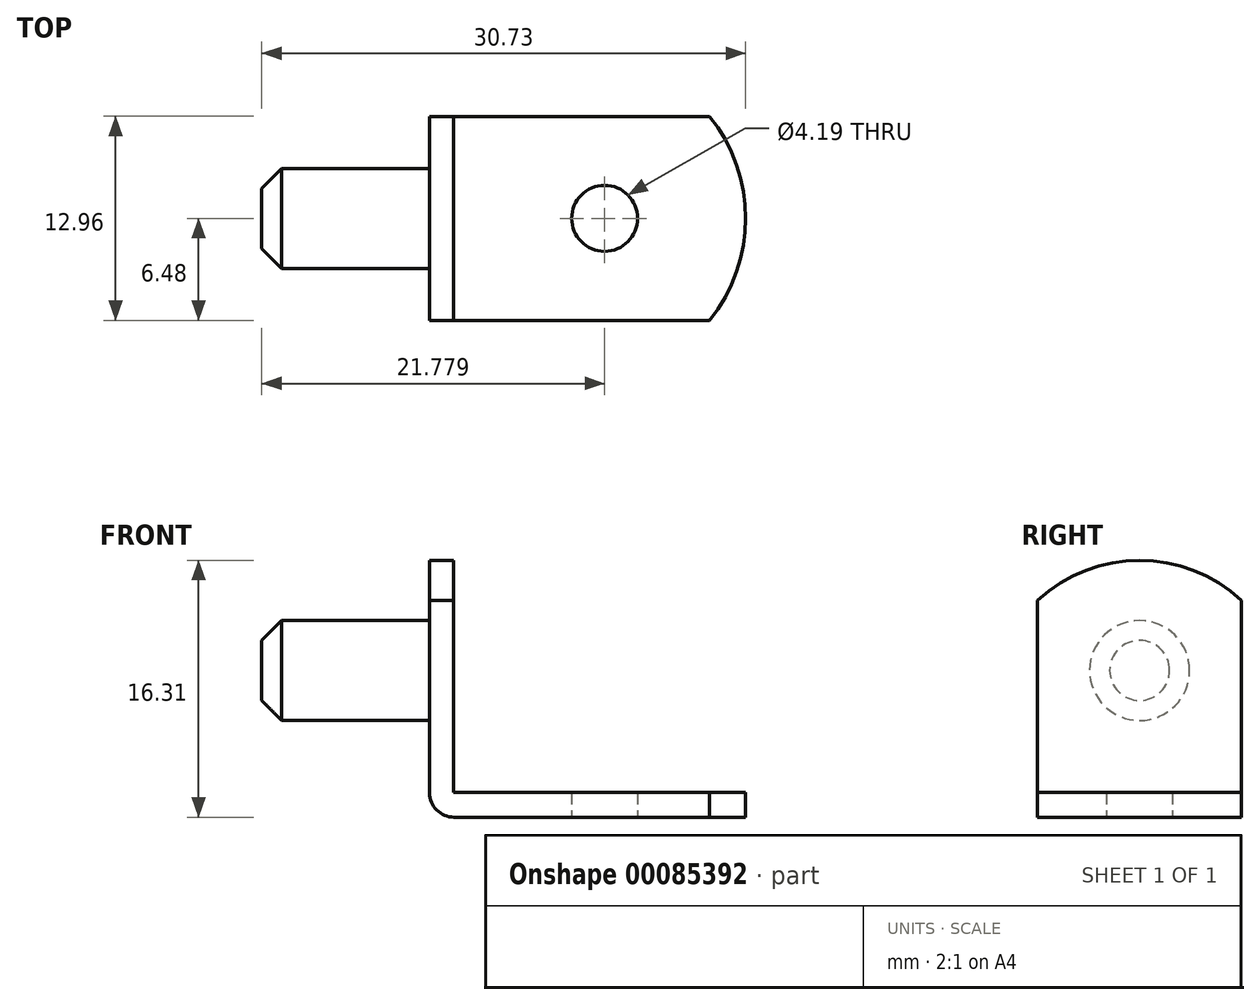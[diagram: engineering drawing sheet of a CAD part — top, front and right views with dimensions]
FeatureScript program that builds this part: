
annotation { "Feature Type Name" : "Feature", "Feature Type Description" : "" }
export const myFeature = defineFeature(function(context is Context, id is Id, definition is map)
    precondition{}
    {
        {
            var Q0;
            Q0=qCreatedBy(makeId("Right.planeOp"),FACE);
            var sketch = newSketch(context, id + "F0", { "sketchPlane" : qUnion([Q0])});
            skLineSegment(sketch, "E0.bottom", {"start": v(-6.48, 6.1) * mm, "end": v(6.48, 6.1) * mm});
            skLineSegment(sketch, "E0.top", {"start": v(-6.48, -6.1) * mm, "end": v(6.48, -6.1) * mm});
            skLineSegment(sketch, "E0.left", {"start": v(-6.48, 6.1) * mm, "end": v(-6.48, -6.1) * mm});
            skLineSegment(sketch, "E0.right", {"start": v(6.48, 6.1) * mm, "end": v(6.48, -6.1) * mm});
            skPoint(sketch, "E0.middle", {"position": v(0, 0) * mm});
            skArc(sketch, "E1", {"start": v(6.48, 6.1) * mm, "mid": v(0, 8.64) * mm, "end": v(-6.48, 6.1) * mm});
            skCircle(sketch, "E2", {"center": v(0, 1.65) * mm, "radius": 3.18 * mm});
            skLineSegment(sketch, "E3.top", {"start": v(-6.48, -7.67) * mm, "end": v(6.48, -7.67) * mm});
            skLineSegment(sketch, "E3.left", {"start": v(-6.48, -6.1) * mm, "end": v(-6.48, -7.67) * mm});
            skLineSegment(sketch, "E3.right", {"start": v(6.48, -6.1) * mm, "end": v(6.48, -7.67) * mm});
            skSolve(sketch);
        }
        {
            var Q0;
            Q0 = qSketchRegion(id + "F0", true);
            var Q1;
            Q1=makeQuery(id+"F0.imprint","IMPRINT",FACE,{"disambiguationData":[TD([[makeQuery(id+"F0.imprint","IMPRINT",EDGE,{"derivedFrom":sQuery(id+"F0.wireOp",EDGE,"E2")}),1.0]])]});
            var Q2;
            Q2=makeQuery(id+"F0.imprint","IMPRINT",FACE,{"disambiguationData":[TD([[makeQuery(id+"F0.imprint","IMPRINT",EDGE,{"derivedFrom":sQuery(id+"F0.wireOp",EDGE,"c23ZDLoS-5MUO-r9MN-FOHE-IyfGmuovY2nj")}),1.0]])]});
            extrude(context, id + "F1", {"entities" : qUnion([Q0, Q1, Q2]), "oppositeDirection" : true, "depth" : 1.52 * mm});
        }
        {
            var Q0;
            Q0=makeQuery(id+"F0.imprint","IMPRINT",FACE,{"disambiguationData":[TD([[makeQuery(id+"F0.imprint","IMPRINT",EDGE,{"derivedFrom":sQuery(id+"F0.wireOp",EDGE,"E2")}),1.0]])]});
            extrude(context, id + "F2", {"entities" : qUnion([Q0]), "operationType" : NewBodyOperationType.ADD, "oppositeDirection" : true, "depth" : 12.2 * mm});
        }
        {
            var Q0;
            Q0=makeQuery(id+"F2.opExtrude","CAP_EDGE",EDGE,{"disambiguationData":[OSD([sQuery(id+"F0.wireOp",EDGE,"E2")])],"isStart":false});
            chamfer(context, id + "F3", {"entities" : qUnion([Q0]), "width" : 1.27 * mm, "tangentPropagation" : true});
        }
        {
            var Q0;
            Q0=makeQuery(id+"F1.opExtrude","SWEPT_FACE",FACE,{"disambiguationData":[OSD([sQuery(id+"F0.wireOp",EDGE,"E3.top")])]});
            cPlane(context, id + "F4", {"entities" : qUnion([Q0]), "cplaneType" : CPlaneType.OFFSET, "offset" : 0 * mm, "width" : 152.4 * mm, "height" : 152.4 * mm});
        }
        {
            var Q0;
            Q0=qCreatedBy(id+"F4.planeOp",FACE);
            var sketch = newSketch(context, id + "F5", { "sketchPlane" : qUnion([Q0])});
            skLineSegment(sketch, "E4.bottom", {"start": v(0, -6.48) * mm, "end": v(16.26, -6.48) * mm});
            skLineSegment(sketch, "E4.top", {"start": v(0, 6.48) * mm, "end": v(16.26, 6.48) * mm});
            skLineSegment(sketch, "E4.left", {"start": v(0, -6.48) * mm, "end": v(0, 6.48) * mm});
            skLineSegment(sketch, "E4.right", {"start": v(16.26, -6.48) * mm, "end": v(16.26, 6.48) * mm});
            skArc(sketch, "E5", {"start": v(16.26, -6.48) * mm, "mid": v(18.54, 0) * mm, "end": v(16.26, 6.48) * mm});
            skCircle(sketch, "E6", {"center": v(9.59, 0) * mm, "radius": 2.1 * mm});
            skSolve(sketch);
        }
        {
            var Q0;
            Q0=makeQuery(id+"F5.imprint","IMPRINT",FACE,{"disambiguationData":[TD([[makeQuery(id+"F5.imprint","IMPRINT",EDGE,{"derivedFrom":sQuery(id+"F5.wireOp",EDGE,"E4.bottom")}),1.0]])]});
            var Q1;
            Q1=makeQuery(id+"F5.imprint","IMPRINT",FACE,{"disambiguationData":[TD([[makeQuery(id+"F5.imprint","IMPRINT",EDGE,{"derivedFrom":sQuery(id+"F5.wireOp",EDGE,"E4.right")}),-1.0]])]});
            extrude(context, id + "F6", {"entities" : qUnion([Q0, Q1]), "operationType" : NewBodyOperationType.ADD, "oppositeDirection" : true, "depth" : 1.57 * mm});
        }
        {
            var Q0;
            Q0=makeQuery(id+"F1.opExtrude","CAP_EDGE",EDGE,{"disambiguationData":[OSD([sQuery(id+"F0.wireOp",EDGE,"E3.top")])],"isStart":false});
            fillet(context, id + "F7", {"entities" : qUnion([Q0]), "radius" : 1.55 * mm, "tangentPropagation" : true, "allowEdgeOverflow" : false});
        }
    });
